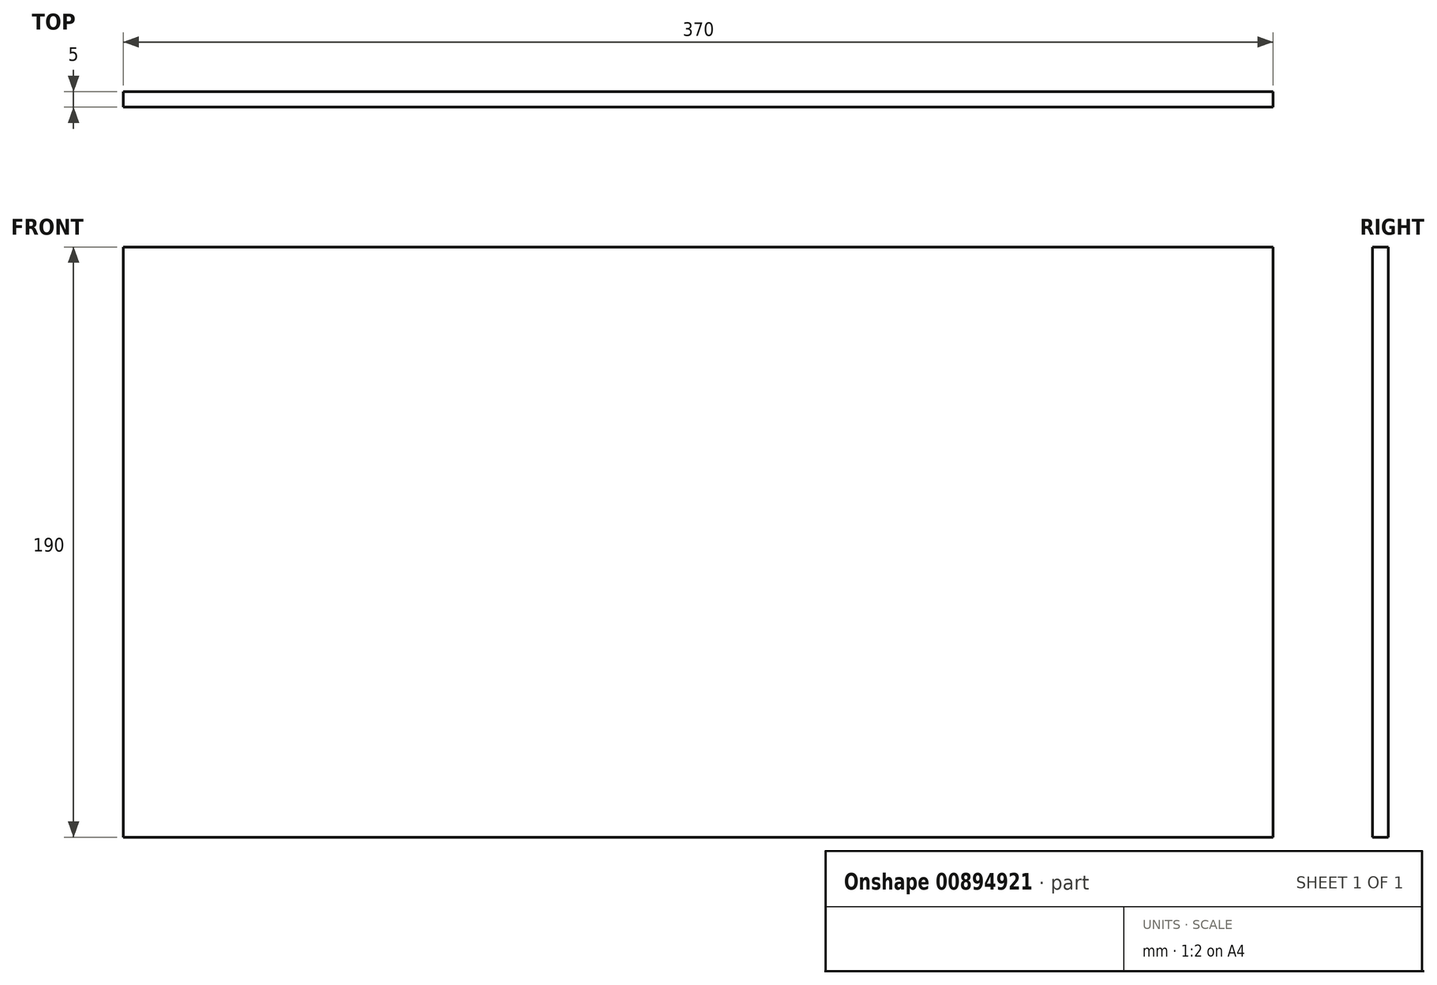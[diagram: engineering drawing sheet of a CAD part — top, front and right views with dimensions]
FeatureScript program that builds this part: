
annotation { "Feature Type Name" : "Feature", "Feature Type Description" : "" }
export const myFeature = defineFeature(function(context is Context, id is Id, definition is map)
    precondition{}
    {
        {
            var Q0;
            Q0=qCreatedBy(makeId("Front.planeOp"),FACE);
            var sketch = newSketch(context, id + "F0", { "sketchPlane" : qUnion([Q0])});
            skLineSegment(sketch, "E0.bottom", {"start": v(0, 0) * mm, "end": v(370, 0) * mm});
            skLineSegment(sketch, "E0.top", {"start": v(0, -190) * mm, "end": v(370, -190) * mm});
            skLineSegment(sketch, "E0.left", {"start": v(0, 0) * mm, "end": v(0, -190) * mm});
            skLineSegment(sketch, "E0.right", {"start": v(370, 0) * mm, "end": v(370, -190) * mm});
            skSolve(sketch);
        }
        {
            var Q0;
            Q0=makeQuery(id+"F0.imprint","IMPRINT",FACE,{"disambiguationData":[TD([[makeQuery(id+"F0.imprint","IMPRINT",EDGE,{"derivedFrom":sQuery(id+"F0.wireOp",EDGE,"E0.bottom")}),-1.0]])]});
            extrude(context, id + "F1", {"entities" : qUnion([Q0]), "depth" : 5 * mm, "offsetDistance" : 25 * mm});
        }
    });
